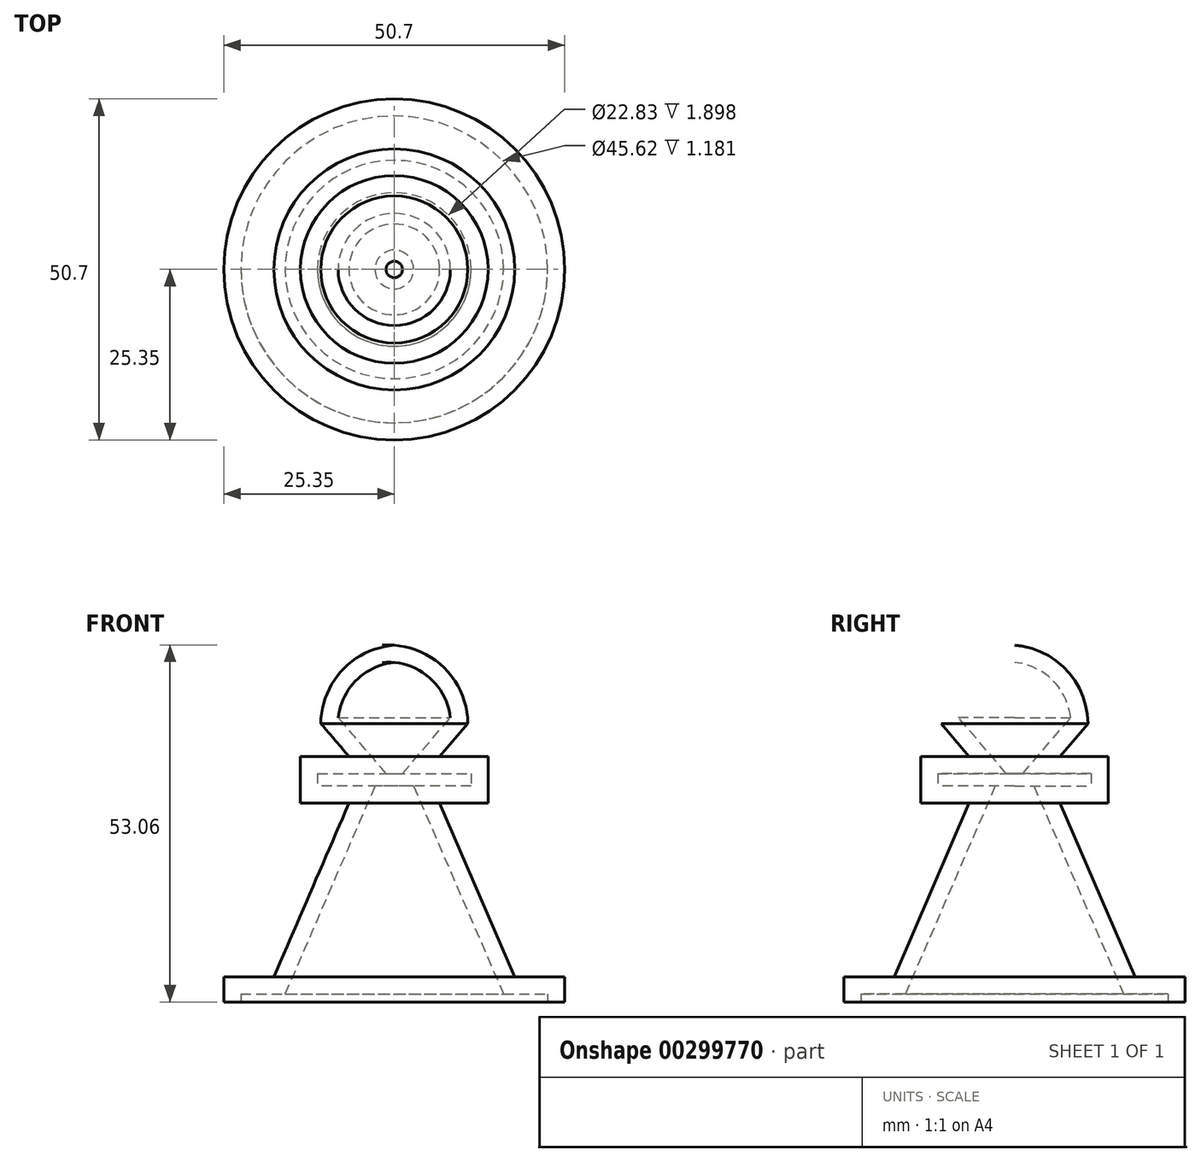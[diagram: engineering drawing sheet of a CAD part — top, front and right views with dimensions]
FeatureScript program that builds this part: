
annotation { "Feature Type Name" : "Feature", "Feature Type Description" : "" }
export const myFeature = defineFeature(function(context is Context, id is Id, definition is map)
    precondition{}
    {
        {
            var Q0;
            Q0=qCreatedBy(makeId("Front.planeOp"),FACE);
            var sketch = newSketch(context, id + "F0", { "sketchPlane" : qUnion([Q0])});
            skLineSegment(sketch, "E0", {"start": v(0, 0) * mm, "end": v(0, 53.03) * mm});
            skArc(sketch, "E1", {"start": v(0, 53.03) * mm, "mid": v(-7.73, 49.34) * mm, "end": v(-10.93, 41.4) * mm});
            skLineSegment(sketch, "E2", {"start": v(-10.93, 41.4) * mm, "end": v(-6.75, 36.52) * mm});
            skLineSegment(sketch, "E3", {"start": v(-6.75, 36.52) * mm, "end": v(-13.96, 36.52) * mm});
            skLineSegment(sketch, "E4", {"start": v(-13.96, 36.52) * mm, "end": v(-13.96, 29.54) * mm});
            skLineSegment(sketch, "E5", {"start": v(-13.96, 29.54) * mm, "end": v(-6.75, 29.54) * mm});
            skLineSegment(sketch, "E6", {"start": v(-6.75, 29.54) * mm, "end": v(-17.9, 3.72) * mm});
            skLineSegment(sketch, "E7", {"start": v(-17.9, 3.72) * mm, "end": v(-25.35, 3.72) * mm});
            skLineSegment(sketch, "E8", {"start": v(-25.35, 3.72) * mm, "end": v(-25.35, 0) * mm});
            skLineSegment(sketch, "E9", {"start": v(-25.35, 0) * mm, "end": v(0, 0) * mm});
            skSolve(sketch);
        }
        {
            var Q0;
            Q0=makeQuery(id+"F0.imprint","IMPRINT",FACE,{"disambiguationData":[TD([[makeQuery(id+"F0.imprint","IMPRINT",EDGE,{"derivedFrom":sQuery(id+"F0.wireOp",EDGE,"E0")}),1.0]])]});
            var Q1;
            Q1=sQuery(id+"F0.wireOp",EDGE,"E0");
            revolve(context, id + "F1", {"entities" : qUnion([Q0]), "axis" : qUnion([Q1]), "revolveType" : RevolveType.FULL});
        }
        {
            var Q0;
            Q0=makeQuery(id+"F1.opRevolve","SWEPT_FACE",FACE,{"disambiguationData":[OSD([sQuery(id+"F0.wireOp",EDGE,"E9")])]});
            shell(context, id + "F2", {"entities" : qUnion([Q0]), "thickness" : 2.54 * mm});
        }
    });
